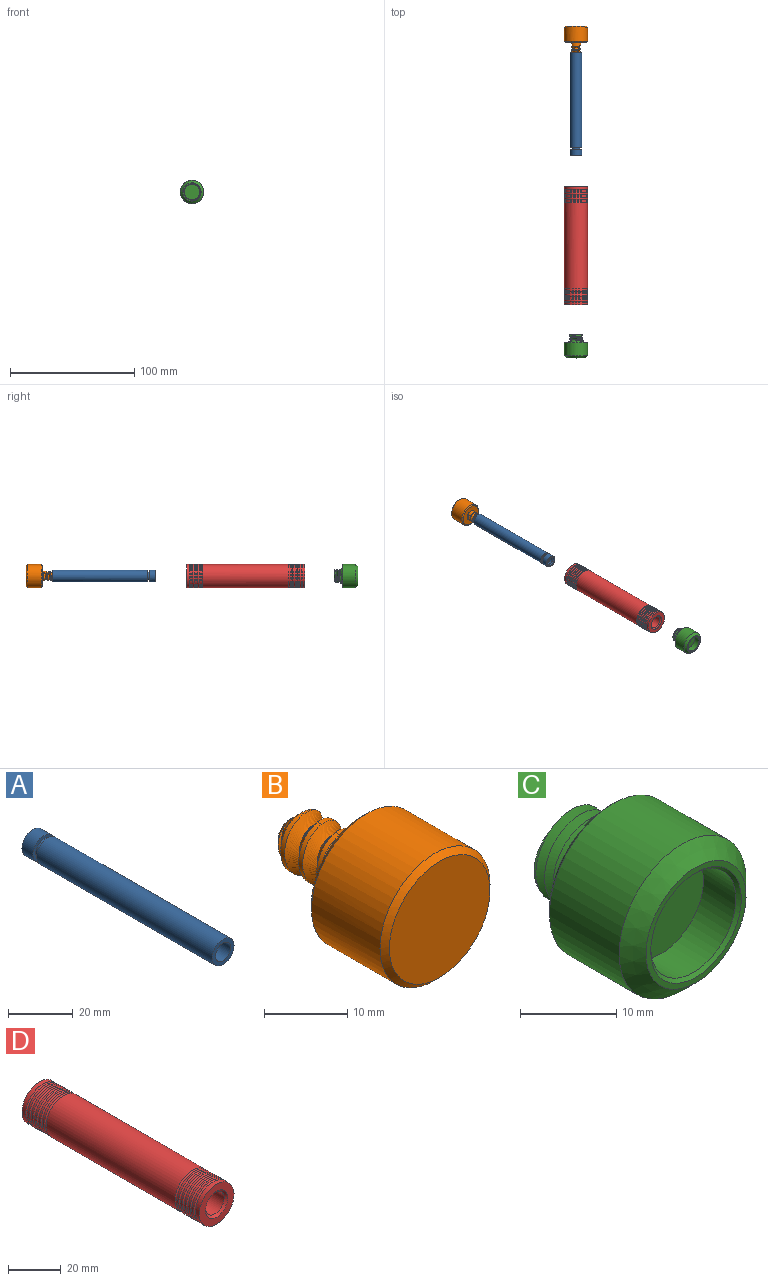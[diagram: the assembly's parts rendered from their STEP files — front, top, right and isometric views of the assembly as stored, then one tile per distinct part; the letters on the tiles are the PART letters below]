
ASSEMBLY  parts=4 mates=4
PART A: 12 faces, bbox 9.5x82.9x9.5 mm
  f0: cylinder r=4.76mm len=76.52mm, axis (0,1,0), area 2289.9mm2, adj f1,f5
  f1: plane 9.53x9.53mm, normal (0,-1,0), area 37mm2, adj f0,f2
  f2: cylinder r=3.3mm len=74mm, axis (0,-1,0), area 1534.4mm2, adj f1,f3
  f3: cone r=0mm half-angle=59deg, axis (0,-1,0), area 39.9mm2, adj f2
  f4: cylinder r=3.57mm len=7.14mm, axis (0,1,0), area 35.9mm2, adj f5,f6
  f5: plane 9.53x9.53mm, normal (0,1,0), area 31.2mm2, adj f0,f4
  f6: plane 9.53x9.53mm, normal (0,-1,0), area 31.2mm2, adj f4,f8
  f7: plane 9.53x9.53mm, normal (0,1,0), area 21mm2, adj f8,f10
  f8: cylinder r=4.76mm len=9.53mm, axis (0,1,0), area 142.9mm2, adj f6,f7
  f9: cylinder r=3mm len=6mm, axis (0,1,0), area 47.1mm2, adj f10,f11
  f10: cone r=3mm half-angle=45deg, axis (0,1,0), area 31.1mm2, adj f7,f9
  f11: cone r=0mm half-angle=59deg, axis (0,1,0), area 33mm2, adj f9
PART B: 14 faces, bbox 18.6x26.6x18.6 mm
  f0: cylinder r=9.32mm len=18.64mm, axis (0,1,0), area 679.4mm2, adj f8,f9
  f1: plane 17.04x17.04mm, normal (0,-1,0), area 228.1mm2, adj f8
  f2: cylinder r=4mm len=8mm, axis (0,1,0), area 57mm2, adj f3,f6,f10,f11,f12
  f3: cylinder r=4mm len=8mm, axis (0,1,0), area 17.1mm2, adj f2,f4,f11,f12
  f4: cylinder r=4mm len=8mm, axis (0,1,0), area 16.8mm2, adj f3,f5,f11,f12,f13
  f5: cylinder r=4mm len=2.94mm, axis (0,1,0), area 0.7mm2, adj f4,f12,f13
  f6: plane 17.04x17.04mm, normal (0,1,0), area 177.9mm2, adj f2,f9
  f7: plane 4x4mm, normal (0,1,0), area 12.6mm2, adj f13
  f8: cone r=8.52mm half-angle=45deg, axis (0,1,0), area 63.4mm2, adj f0,f1
  f9: cone r=9.32mm half-angle=45deg, axis (0,-1,0), area 63.4mm2, adj f0,f6
  f10: plane 2.37x1.77mm, normal (0.5,0,0.86), area 2.4mm2, adj f2,f11,f12
  f11: bspline ~11.67x10.33mm, area 135.5mm2, adj f2,f3,f4,f10,f12,f13
  f12: bspline ~11.67x10.33mm, area 103.6mm2, adj f2,f3,f4,f5,f10,f11,f13
  f13: cone r=2mm half-angle=45deg, axis (0,-1,0), area 33.7mm2, adj f4,f5,f7,f11,f12
PART C: 16 faces, bbox 19.6x20.8x19.6 mm
  f0: cylinder r=6mm len=12mm, axis (0,1,0), area 7.1mm2, adj f4,f6,f14,f15
  f1: cylinder r=9.32mm len=18.64mm, axis (0,-1,0), area 598.5mm2, adj f3,f5
  f2: plane 14.68x14.68mm, normal (0,-1,0), area 30.4mm2, adj f3,f13
  f3: cone r=9.32mm half-angle=45deg, axis (0,1,0), area 146.7mm2, adj f1,f2
  f4: plane 17.79x17.79mm, normal (0,1,0), area 132.4mm2, adj f0,f5,f6,f14
  f5: cone r=8.82mm half-angle=45deg, axis (0,-1,0), area 40.3mm2, adj f1,f4
  f6: plane 1.74x1.64mm, normal (0,0,1), area 1.5mm2, adj f0,f4,f7,f8,f9,f14,f15
  f7: bspline ~12.4x10.74mm, area 172.1mm2, adj f6,f8,f9,f10
  f8: bspline ~13.86x12mm, area 5.2mm2, adj f6,f7,f14,f15
  f9: bspline ~12.4x10.74mm, area 152.1mm2, adj f6,f7,f10
  f10: plane 10.62x10.61mm, normal (0,1,0), area 73.2mm2, adj f7,f9
  f11: cylinder r=6.25mm len=12.5mm, axis (0,-1,0), area 186.7mm2, adj f12,f13
  f12: plane 12.5x12.5mm, normal (0,-1,0), area 122.7mm2, adj f11
  f13: cone r=6.25mm half-angle=45deg, axis (0,-1,0), area 22.9mm2, adj f2,f11
  f14: bspline ~12x6.16mm, area 14mm2, adj f0,f4,f6,f8,f15
  f15: bspline ~12x6.21mm, area 19.2mm2, adj f0,f6,f8,f14
PART D: 29 faces, bbox 20.2x95.3x20.2 mm
  f0: cylinder r=9.32mm len=69.25mm, axis (0,-1,0), area 4056mm2, adj f19,f23
  f1: cylinder r=9.32mm len=18.64mm, axis (0,-1,0), area 58.6mm2, adj f23,f24
  f2: cylinder r=9.32mm len=18.64mm, axis (0,-1,0), area 58.6mm2, adj f24,f25
  f3: cylinder r=9.32mm len=18.64mm, axis (0,-1,0), area 58.6mm2, adj f25,f26
  f4: cylinder r=9.32mm len=18.64mm, axis (0,-1,0), area 58.6mm2, adj f26,f27
  f5: cylinder r=9.32mm len=18.64mm, axis (0,-1,0), area 58.6mm2, adj f27,f28
  f6: cylinder r=9.32mm len=18.64mm, axis (0,-1,0), area 117.1mm2, adj f14,f28
  f7: cylinder r=9.32mm len=18.64mm, axis (0,-1,0), area 58.6mm2, adj f19,f20
  f8: cylinder r=9.32mm len=18.64mm, axis (0,-1,0), area 58.6mm2, adj f20,f21
  f9: cylinder r=9.32mm len=18.64mm, axis (0,-1,0), area 58.6mm2, adj f21,f22
  f10: cylinder r=9.32mm len=18.64mm, axis (0,-1,0), area 58.6mm2, adj f18,f22
  f11: cylinder r=9.32mm len=18.64mm, axis (0,-1,0), area 58.6mm2, adj f17,f18
  f12: cylinder r=5mm len=94.25mm, axis (0,-1,0), area 2963.3mm2, adj f14,f16
  f13: cylinder r=9.32mm len=18.64mm, axis (0,-1,0), area 117.1mm2, adj f15,f17
  f14: plane 18.64x18.64mm, normal (0,1,0), area 194.3mm2, adj f6,f12
  f15: plane 18.64x18.64mm, normal (0,-1,0), area 159.9mm2, adj f13,f16
  f16: cone r=3.3mm half-angle=45deg, axis (0,-1,0), area 48.7mm2, adj f12,f15
  f17: torus R=9.32mm, axis (0,1,0), area 88.8mm2, adj f11,f13
  f18: torus R=9.32mm, axis (0,1,0), area 88.8mm2, adj f10,f11
  f19: torus R=9.32mm, axis (0,1,0), area 88.8mm2, adj f0,f7
  f20: torus R=9.32mm, axis (0,1,0), area 88.8mm2, adj f7,f8
  f21: torus R=9.32mm, axis (0,1,0), area 88.8mm2, adj f8,f9
  f22: torus R=9.32mm, axis (0,1,0), area 88.8mm2, adj f9,f10
  f23: torus R=9.32mm, axis (0,-1,0), area 88.8mm2, adj f0,f1
  f24: torus R=9.32mm, axis (0,-1,0), area 88.8mm2, adj f1,f2
  f25: torus R=9.32mm, axis (0,-1,0), area 88.8mm2, adj f2,f3
  f26: torus R=9.32mm, axis (0,-1,0), area 88.8mm2, adj f3,f4
  f27: torus R=9.32mm, axis (0,-1,0), area 88.8mm2, adj f4,f5
  f28: torus R=9.32mm, axis (0,-1,0), area 88.8mm2, adj f5,f6
PLACE A rot(axis=(0,0,-1),180deg) t=(53.42,59.16,-17.47)mm
PLACE B rot(axis=(0.94,0,-0.35),180deg) t=(-75.42,138.06,84.05)mm
PLACE C rot(axis=(0,-1,0),90deg) t=(-52.31,-37.15,21.59)mm
PLACE D rot(axis=(0,1,0),0deg) t=(-13.65,-61.2,10.07)mm fixed
MATE parallel C.f4 <-> D.f0  axis (0,1,0) through (-52.34,-91.2,21.56)mm
MATE cylindrical B.f0 <-> A.f0  axis (0,-1,0) through (-52.34,150.26,21.56)mm
MATE slider A.f0 <-> D.f0  axis (0,1,0) through (-52.34,142.06,21.56)mm
MATE cylindrical C.f4 <-> D.f0  axis (0,1,0) through (-52.34,-91.2,21.56)mm
